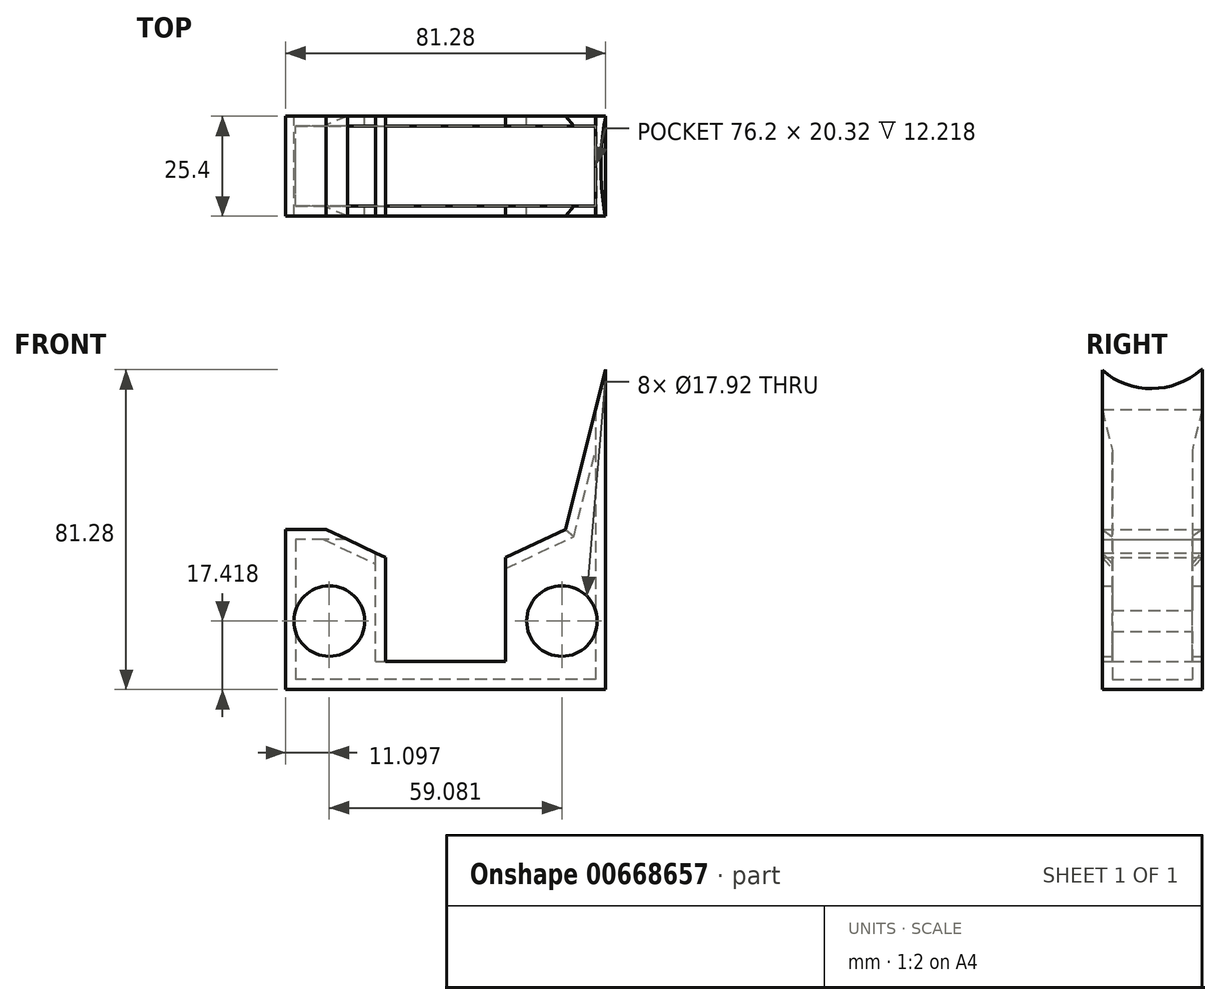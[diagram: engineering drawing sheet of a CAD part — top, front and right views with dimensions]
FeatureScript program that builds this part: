
annotation { "Feature Type Name" : "Feature", "Feature Type Description" : "" }
export const myFeature = defineFeature(function(context is Context, id is Id, definition is map)
    precondition{}
    {
        {
            var Q0;
            Q0=qCreatedBy(makeId("Front.planeOp"),FACE);
            var sketch = newSketch(context, id + "F0", { "sketchPlane" : qUnion([Q0])});
            skLineSegment(sketch, "E0.bottom", {"start": v(40.64, 40.64) * mm, "end": v(-40.64, 40.64) * mm});
            skLineSegment(sketch, "E0.top", {"start": v(40.64, -40.64) * mm, "end": v(-40.64, -40.64) * mm});
            skLineSegment(sketch, "E0.left", {"start": v(40.64, 40.64) * mm, "end": v(40.64, -40.64) * mm});
            skLineSegment(sketch, "E0.right", {"start": v(-40.64, 40.64) * mm, "end": v(-40.64, -40.64) * mm});
            skPoint(sketch, "E0.middle", {"position": v(0, 0) * mm});
            skLineSegment(sketch, "E1.bottom", {"start": v(-15.24, -33.48) * mm, "end": v(15.24, -33.48) * mm});
            skLineSegment(sketch, "E1.top", {"start": v(-15.24, 33.48) * mm, "end": v(15.24, 33.48) * mm});
            skLineSegment(sketch, "E1.left", {"start": v(-15.24, -33.48) * mm, "end": v(-15.24, 33.48) * mm});
            skLineSegment(sketch, "E1.right", {"start": v(15.24, -33.48) * mm, "end": v(15.24, 33.48) * mm});
            skLineSegment(sketch, "E2", {"start": v(-40.64, 40.64) * mm, "end": v(-30.4, 0) * mm});
            skLineSegment(sketch, "E3", {"start": v(-30.4, 0) * mm, "end": v(-40.64, 40.64) * mm});
            skLineSegment(sketch, "E4", {"start": v(40.64, 40.64) * mm, "end": v(30.4, 0) * mm});
            skLineSegment(sketch, "E5", {"start": v(-30.4, 0) * mm, "end": v(-40.64, 0) * mm});
            skLineSegment(sketch, "E6", {"start": v(-40.64, 0) * mm, "end": v(30.4, 0) * mm});
            skLineSegment(sketch, "E7", {"start": v(30.4, 0) * mm, "end": v(40.64, 0) * mm});
            skPoint(sketch, "E8", {"position": v(-15.24, -7.07) * mm});
            skPoint(sketch, "E9", {"position": v(15.24, -7.07) * mm});
            skLineSegment(sketch, "E10", {"start": v(-30.4, 0) * mm, "end": v(-15.24, -7.07) * mm});
            skLineSegment(sketch, "E11", {"start": v(15.24, -7.07) * mm, "end": v(30.4, 0) * mm});
            skPoint(sketch, "E12", {"position": v(-25.8, -10.17) * mm});
            skPoint(sketch, "E13", {"position": v(25.2, -11.76) * mm});
            skLineSegment(sketch, "E14", {"start": v(-15.24, -7.07) * mm, "end": v(-15.24, -33.48) * mm});
            skSolve(sketch);
        }
        {
            var Q0;
            {var subQ4=sQuery(id+"F0.wireOp",EDGE,"E0.top");Q0=makeQuery(id+"F0.imprint","IMPRINT",FACE,{"disambiguationData":[TD([[makeQuery(id+"F0.imprint","IMPRINT",EDGE,{"derivedFrom":subQ4}),-1.0]])]});}
            var Q1;
            {var subQ0=sQuery(id+"F0.wireOp",EDGE,"E3");Q1=makeQuery(id+"F0.imprint","IMPRINT",FACE,{"disambiguationData":[TD([[makeQuery(id+"F0.imprint","IMPRINT",EDGE,{"derivedFrom":subQ0}),1.0]])]});}
            var Q2;
            {var subQ0=sQuery(id+"F0.wireOp",EDGE,"E4");Q2=makeQuery(id+"F0.imprint","IMPRINT",FACE,{"disambiguationData":[TD([[makeQuery(id+"F0.imprint","IMPRINT",EDGE,{"derivedFrom":subQ0}),1.0]])]});}
            extrude(context, id + "F1", {"entities" : qUnion([Q0, Q1, Q2]), "depth" : 25.4 * mm, "offsetDistance" : 25.4 * mm});
        }
        {
            var Q0;
            Q0=makeQuery(id+"F1.opExtrude","SWEPT_FACE",FACE,{"disambiguationData":[OSD([sQuery(id+"F0.wireOp",EDGE,"E4")])]});
            var Q1;
            Q1=makeQuery(id+"F1.opExtrude","SWEPT_FACE",FACE,{"disambiguationData":[OSD([sQuery(id+"F0.wireOp",EDGE,"E11")])]});
            var Q2;
            Q2=makeQuery(id+"F1.opExtrude","SWEPT_FACE",FACE,{"disambiguationData":[OSD([sQuery(id+"F0.wireOp",EDGE,"E1.right")])]});
            var Q3;
            Q3=makeQuery(id+"F1.opExtrude","SWEPT_FACE",FACE,{"disambiguationData":[OSD([sQuery(id+"F0.wireOp",EDGE,"E1.bottom")])]});
            var Q4;
            Q4=makeQuery(id+"F1.opExtrude","SWEPT_FACE",FACE,{"disambiguationData":[OSD([sQuery(id+"F0.wireOp",EDGE,"E3")])]});
            var Q5;
            Q5=makeQuery(id+"F1.opExtrude","SWEPT_FACE",FACE,{"disambiguationData":[OSD([sQuery(id+"F0.wireOp",EDGE,"E10")])]});
            var Q6;
            Q6=makeQuery(id+"F1.opExtrude","SWEPT_FACE",FACE,{"disambiguationData":[OSD([sQuery(id+"F0.wireOp",EDGE,"E14")])]});
            shell(context, id + "F2", {"entities" : qUnion([Q0, Q1, Q2, Q3, Q4, Q5, Q6]), "thickness" : 2.54 * mm});
        }
        {
            var Q0;
            Q0=qCreatedBy(makeId("Front.planeOp"),FACE);
            var sketch = newSketch(context, id + "F3", { "sketchPlane" : qUnion([Q0])});
            skCircle(sketch, "E15", {"center": v(-29.54, -23.22) * mm, "radius": 8.96 * mm});
            skCircle(sketch, "E16", {"center": v(29.54, -23.22) * mm, "radius": 8.96 * mm});
            skSolve(sketch);
        }
        {
            var Q0;
            Q0=makeQuery(id+"F3.imprint","IMPRINT",FACE,{"disambiguationData":[TD([[makeQuery(id+"F3.imprint","IMPRINT",EDGE,{"derivedFrom":sQuery(id+"F3.wireOp",EDGE,"E15")}),1.0]])]});
            var Q1;
            Q1=makeQuery(id+"F3.imprint","IMPRINT",FACE,{"disambiguationData":[TD([[makeQuery(id+"F3.imprint","IMPRINT",EDGE,{"derivedFrom":sQuery(id+"F3.wireOp",EDGE,"E16")}),1.0]])]});
            extrude(context, id + "F4", {"entities" : qUnion([Q0, Q1]), "operationType" : NewBodyOperationType.REMOVE, "depth" : 105.4 * mm, "offsetDistance" : 25.4 * mm});
        }
        {
            var Q0;
            {var subQ0=sQuery(id+"F0.wireOp",EDGE,"E3");Q0=makeQuery(id+"F2.opShell","OFFSET_EDGE",EDGE,{"disambiguationData":[OSD([subQ0]),TDD([makeQuery(id+"F1.opExtrude","CAP_EDGE",EDGE,{"disambiguationData":[OSD([subQ0])],"isStart":false})])]});}
            var Q1;
            {var subQ0=sQuery(id+"F0.wireOp",EDGE,"E10");Q1=makeQuery(id+"F2.opShell","OFFSET_EDGE",EDGE,{"disambiguationData":[OSD([subQ0]),TDD([makeQuery(id+"F1.opExtrude","CAP_EDGE",EDGE,{"disambiguationData":[OSD([subQ0])],"isStart":false})])]});}
            var Q2;
            {var subQ0=sQuery(id+"F0.wireOp",EDGE,"E3");Q2=makeQuery(id+"F2.opShell","OFFSET_EDGE",EDGE,{"disambiguationData":[OSD([subQ0]),TDD([makeQuery(id+"F1.opExtrude","CAP_EDGE",EDGE,{"disambiguationData":[OSD([subQ0])],"isStart":true})])]});}
            var Q3;
            {var subQ0=sQuery(id+"F0.wireOp",EDGE,"E10");Q3=makeQuery(id+"F2.opShell","OFFSET_EDGE",EDGE,{"disambiguationData":[OSD([subQ0]),TDD([makeQuery(id+"F1.opExtrude","CAP_EDGE",EDGE,{"disambiguationData":[OSD([subQ0])],"isStart":true})])]});}
            var Q4;
            {var subQ0=sQuery(id+"F0.wireOp",EDGE,"E11");Q4=makeQuery(id+"F2.opShell","OFFSET_EDGE",EDGE,{"disambiguationData":[OSD([subQ0]),TDD([makeQuery(id+"F1.opExtrude","CAP_EDGE",EDGE,{"disambiguationData":[OSD([subQ0])],"isStart":true})])]});}
            var Q5;
            {var subQ0=sQuery(id+"F0.wireOp",EDGE,"E4");Q5=makeQuery(id+"F2.opShell","OFFSET_EDGE",EDGE,{"disambiguationData":[OSD([subQ0]),TDD([makeQuery(id+"F1.opExtrude","CAP_EDGE",EDGE,{"disambiguationData":[OSD([subQ0])],"isStart":true})])]});}
            var Q6;
            {var subQ0=sQuery(id+"F0.wireOp",EDGE,"E4");Q6=makeQuery(id+"F2.opShell","OFFSET_EDGE",EDGE,{"disambiguationData":[OSD([subQ0]),TDD([makeQuery(id+"F1.opExtrude","CAP_EDGE",EDGE,{"disambiguationData":[OSD([subQ0])],"isStart":false})])]});}
            var Q7;
            {var subQ0=sQuery(id+"F0.wireOp",EDGE,"E11");Q7=makeQuery(id+"F2.opShell","OFFSET_EDGE",EDGE,{"disambiguationData":[OSD([subQ0]),TDD([makeQuery(id+"F1.opExtrude","CAP_EDGE",EDGE,{"disambiguationData":[OSD([subQ0])],"isStart":false})])]});}
            chamfer(context, id + "F5", {"entities" : qUnion([Q0, Q1, Q2, Q3, Q4, Q5, Q6, Q7]), "width" : 2.54 * mm, "tangentPropagation" : true});
        }
        {
            var Q0;
            Q0=qCreatedBy(makeId("Right.planeOp"),FACE);
            var sketch = newSketch(context, id + "F6", { "sketchPlane" : qUnion([Q0])});
            skCircle(sketch, "E17", {"center": v(-12.9, 54.98) * mm, "radius": 19.13 * mm});
            skSolve(sketch);
        }
        {
            var Q0;
            Q0 = qSketchRegion(id + "F6", true);
            extrude(context, id + "F7", {"entities" : qUnion([Q0]), "operationType" : NewBodyOperationType.REMOVE, "oppositeDirection" : true, "depth" : 254 * mm, "offsetDistance" : 25.4 * mm, "hasSecondDirection" : true, "secondDirectionOppositeDirection" : false, "secondDirectionDepth" : 170.94 * mm});
        }
    });
